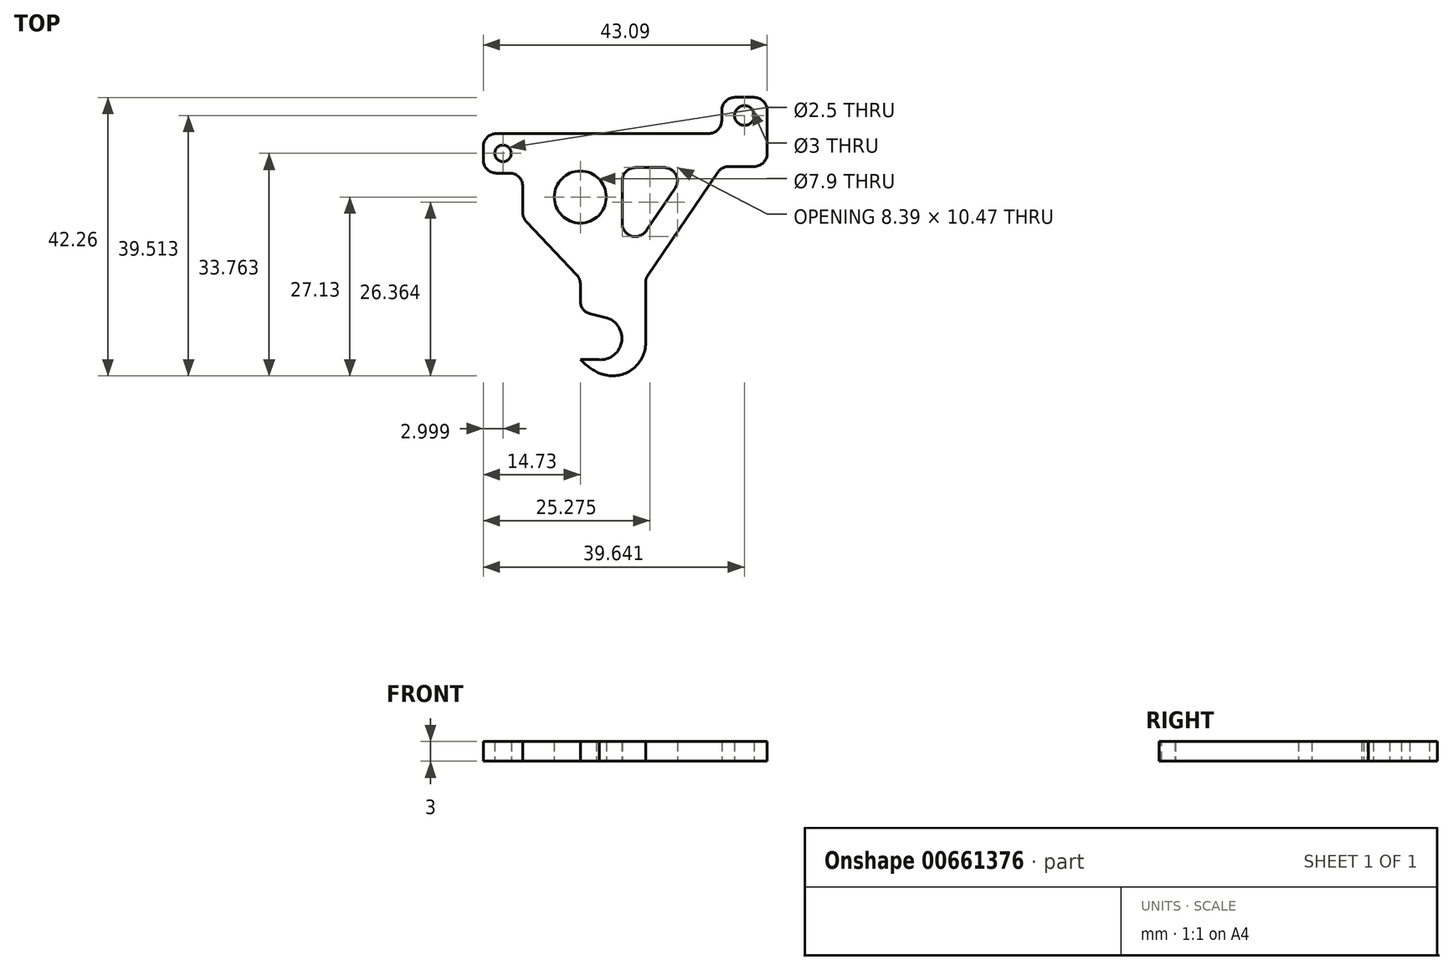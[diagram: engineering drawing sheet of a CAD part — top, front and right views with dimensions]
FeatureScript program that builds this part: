
annotation { "Feature Type Name" : "Feature", "Feature Type Description" : "" }
export const myFeature = defineFeature(function(context is Context, id is Id, definition is map)
    precondition{}
    {
        {
            var Q0;
            Q0=qCreatedBy(makeId("Top.planeOp"),FACE);
            var sketch = newSketch(context, id + "F0", { "sketchPlane" : qUnion([Q0])});
            skLineSegment(sketch, "E0.bottom", {"start": v(9.91, -14.86) * mm, "end": v(4.02, -14.86) * mm});
            skLineSegment(sketch, "E0.top", {"start": v(21.46, 22.01) * mm, "end": v(-8.73, 22.01) * mm});
            skPoint(sketch, "E0.middle", {"position": v(0, 0) * mm});
            skCircle(sketch, "E1", {"center": v(0, 12.38) * mm, "radius": 3.95 * mm});
            skLineSegment(sketch, "E2", {"start": v(9.91, -11.44) * mm, "end": v(9.91, -14.86) * mm});
            skLineSegment(sketch, "E3", {"start": v(-8.73, 9.2) * mm, "end": v(-8.76, 9.2) * mm});
            skLineSegment(sketch, "E4", {"start": v(28.36, 17.01) * mm, "end": v(21.46, 17.01) * mm});
            skLineSegment(sketch, "E5", {"start": v(21.46, 17.01) * mm, "end": v(9.91, 0) * mm});
            skLineSegment(sketch, "E6", {"start": v(9.91, 0) * mm, "end": v(9.91, -11.44) * mm});
            skLineSegment(sketch, "E7", {"start": v(0, -13.25) * mm, "end": v(0, -12.25) * mm});
            skLineSegment(sketch, "E8", {"start": v(0, -5) * mm, "end": v(0, 0) * mm});
            skLineSegment(sketch, "E9", {"start": v(0, 0) * mm, "end": v(-8.73, 9.2) * mm});
            skLineSegment(sketch, "E10", {"start": v(-8.73, 17.01) * mm, "end": v(-8.73, 9.2) * mm});
            skArc(sketch, "E11", {"start": v(2.43, -12.25) * mm, "mid": v(6.24, -9.75) * mm, "end": v(3.8, -5.9) * mm});
            skLineSegment(sketch, "E12", {"start": v(3.7, -12.25) * mm, "end": v(0, -12.25) * mm});
            skLineSegment(sketch, "E13", {"start": v(0, -5) * mm, "end": v(3.8, -5.9) * mm});
            skLineSegment(sketch, "E14", {"start": v(0, -13.25) * mm, "end": v(4.02, -14.86) * mm});
            skLineSegment(sketch, "E15.2", {"start": v(16.52, 16.85) * mm, "end": v(6.35, 1.87) * mm});
            skLineSegment(sketch, "E16", {"start": v(16.52, 16.85) * mm, "end": v(6.35, 16.85) * mm});
            skLineSegment(sketch, "E17", {"start": v(6.35, 16.85) * mm, "end": v(6.35, 1.87) * mm});
            skLineSegment(sketch, "E18.bottom", {"start": v(-8.73, 22.01) * mm, "end": v(-14.73, 22.01) * mm});
            skLineSegment(sketch, "E18.top", {"start": v(-8.73, 16.01) * mm, "end": v(-14.73, 16.01) * mm});
            skLineSegment(sketch, "E18.left", {"start": v(-8.73, 17.01) * mm, "end": v(-8.73, 16.01) * mm});
            skLineSegment(sketch, "E18.right", {"start": v(-14.73, 22.01) * mm, "end": v(-14.73, 16.01) * mm});
            skCircle(sketch, "E19", {"center": v(-11.73, 19.01) * mm, "radius": 1.25 * mm});
            skLineSegment(sketch, "E20.top", {"start": v(21.46, 27.51) * mm, "end": v(28.36, 27.51) * mm});
            skLineSegment(sketch, "E20.left", {"start": v(21.46, 22.01) * mm, "end": v(21.46, 27.51) * mm});
            skLineSegment(sketch, "E20.right", {"start": v(28.36, 22.01) * mm, "end": v(28.36, 27.51) * mm});
            skLineSegment(sketch, "E21", {"start": v(28.36, 22.01) * mm, "end": v(28.36, 17.01) * mm});
            skCircle(sketch, "E22", {"center": v(24.91, 24.76) * mm, "radius": 1.5 * mm});
            skPoint(sketch, "E22.centerSnap0", {"position": v(24.91, 27.51) * mm});
            skPoint(sketch, "E22.centerSnap1", {"position": v(21.46, 24.76) * mm});
            skSolve(sketch);
        }
        {
            var Q0;
            Q0=makeQuery(id+"F0.imprint","IMPRINT",FACE,{"disambiguationData":[TD([[makeQuery(id+"F0.imprint","IMPRINT",EDGE,{"derivedFrom":sQuery(id+"F0.wireOp",EDGE,"E0.top")}),1.0]])]});
            extrude(context, id + "F1", {"entities" : qUnion([Q0]), "depth" : 3 * mm, "offsetDistance" : 25 * mm});
        }
        {
            var Q0;
            Q0=makeQuery(id+"F1.opExtrude","SWEPT_EDGE",EDGE,{"disambiguationData":[OSD([sQuery(id+"F0.wireOp",EDGE,"E0.bottom"),sQuery(id+"F0.wireOp",EDGE,"E14")])]});
            fillet(context, id + "F2", {"entities" : qUnion([Q0]), "radius" : 10 * mm, "tangentPropagation" : true, "allowEdgeOverflow" : false});
        }
        {
            var Q0;
            Q0=makeQuery(id+"F1.opExtrude","SWEPT_EDGE",EDGE,{"disambiguationData":[OSD([sQuery(id+"F0.wireOp",EDGE,"E0.top"),sQuery(id+"F0.wireOp",EDGE,"E0.left")])]});
            var Q1;
            Q1=makeQuery(id+"F1.opExtrude","SWEPT_EDGE",EDGE,{"disambiguationData":[OSD([sQuery(id+"F0.wireOp",EDGE,"E0.top"),sQuery(id+"F0.wireOp",EDGE,"pHyUVdDd-3h7J-JCKs-Me8h-KnZJbw5tkJAh")])]});
            var Q2;
            Q2=makeQuery(id+"F1.opExtrude","SWEPT_EDGE",EDGE,{"disambiguationData":[OSD([sQuery(id+"F0.wireOp",EDGE,"OhQo3RvB-VFTn-GXlj-3DeX-jnrqFRKcEsYa"),sQuery(id+"F0.wireOp",EDGE,"pHyUVdDd-3h7J-JCKs-Me8h-KnZJbw5tkJAh")])]});
            var Q3;
            Q3=makeQuery(id+"F1.opExtrude","SWEPT_EDGE",EDGE,{"disambiguationData":[OSD([sQuery(id+"F0.wireOp",EDGE,"E10"),sQuery(id+"F0.wireOp",EDGE,"OhQo3RvB-VFTn-GXlj-3DeX-jnrqFRKcEsYa")])]});
            var Q4;
            Q4=makeQuery(id+"F1.opExtrude","SWEPT_EDGE",EDGE,{"disambiguationData":[OSD([sQuery(id+"F0.wireOp",EDGE,"E4"),sQuery(id+"F0.wireOp",EDGE,"E5")])]});
            var Q5;
            Q5=makeQuery(id+"F1.opExtrude","SWEPT_EDGE",EDGE,{"disambiguationData":[OSD([sQuery(id+"F0.wireOp",EDGE,"E9"),sQuery(id+"F0.wireOp",EDGE,"E10")])]});
            var Q6;
            Q6=makeQuery(id+"F1.opExtrude","SWEPT_EDGE",EDGE,{"disambiguationData":[OSD([sQuery(id+"F0.wireOp",EDGE,"E8"),sQuery(id+"F0.wireOp",EDGE,"E9")])]});
            var Q7;
            Q7=makeQuery(id+"F1.opExtrude","SWEPT_EDGE",EDGE,{"disambiguationData":[OSD([sQuery(id+"F0.wireOp",EDGE,"E8"),sQuery(id+"F0.wireOp",EDGE,"E13")])]});
            var Q8;
            Q8=makeQuery(id+"F1.opExtrude","SWEPT_EDGE",EDGE,{"disambiguationData":[OSD([sQuery(id+"F0.wireOp",EDGE,"E5"),sQuery(id+"F0.wireOp",EDGE,"E6")])]});
            var Q9;
            Q9=makeQuery(id+"F1.opExtrude","SWEPT_EDGE",EDGE,{"disambiguationData":[OSD([sQuery(id+"F0.wireOp",EDGE,"E0.left"),sQuery(id+"F0.wireOp",EDGE,"E4")])]});
            var Q10;
            Q10=makeQuery(id+"F1.opExtrude","SWEPT_EDGE",EDGE,{"disambiguationData":[OSD([sQuery(id+"F0.wireOp",EDGE,"E16"),sQuery(id+"F0.wireOp",EDGE,"E17")])]});
            var Q11;
            Q11=makeQuery(id+"F1.opExtrude","SWEPT_EDGE",EDGE,{"disambiguationData":[OSD([sQuery(id+"F0.wireOp",EDGE,"E15.2"),sQuery(id+"F0.wireOp",EDGE,"E16")])]});
            var Q12;
            Q12=makeQuery(id+"F1.opExtrude","SWEPT_EDGE",EDGE,{"disambiguationData":[OSD([sQuery(id+"F0.wireOp",EDGE,"E15.2"),sQuery(id+"F0.wireOp",EDGE,"E17")])]});
            var Q13;
            Q13=makeQuery(id+"F1.opExtrude","SWEPT_EDGE",EDGE,{"disambiguationData":[OSD([sQuery(id+"F0.wireOp",EDGE,"E18.top"),sQuery(id+"F0.wireOp",EDGE,"E18.right")])]});
            var Q14;
            Q14=makeQuery(id+"F1.opExtrude","SWEPT_EDGE",EDGE,{"disambiguationData":[OSD([sQuery(id+"F0.wireOp",EDGE,"E18.bottom"),sQuery(id+"F0.wireOp",EDGE,"E18.right")])]});
            var Q15;
            Q15=makeQuery(id+"F1.opExtrude","SWEPT_EDGE",EDGE,{"disambiguationData":[OSD([sQuery(id+"F0.wireOp",EDGE,"Wf6xNexR-8VgF-dvem-LY5D-CjuGMFQnJtrr"),sQuery(id+"F0.wireOp",EDGE,"B4st1OD0-YX5B-bgBp-xqhk-wKI3aAEfzf1H")])]});
            var Q16;
            Q16=makeQuery(id+"F1.opExtrude","SWEPT_EDGE",EDGE,{"disambiguationData":[OSD([sQuery(id+"F0.wireOp",EDGE,"B4st1OD0-YX5B-bgBp-xqhk-wKI3aAEfzf1H"),sQuery(id+"F0.wireOp",EDGE,"RDjMmuDR-6cde-Gaga-eYnt-srqOp1SnWC0k")])]});
            var Q17;
            Q17=makeQuery(id+"F1.opExtrude","SWEPT_EDGE",EDGE,{"disambiguationData":[OSD([sQuery(id+"F0.wireOp",EDGE,"E20.top"),sQuery(id+"F0.wireOp",EDGE,"E20.right")])]});
            var Q18;
            Q18=makeQuery(id+"F1.opExtrude","SWEPT_EDGE",EDGE,{"disambiguationData":[OSD([sQuery(id+"F0.wireOp",EDGE,"E20.top"),sQuery(id+"F0.wireOp",EDGE,"E20.left")])]});
            fillet(context, id + "F3", {"entities" : qUnion([Q0, Q1, Q2, Q3, Q4, Q5, Q6, Q7, Q8, Q9, Q10, Q11, Q12, Q13, Q14, Q15, Q16, Q17, Q18]), "radius" : 2 * mm, "tangentPropagation" : true, "allowEdgeOverflow" : false});
        }
        {
            var Q0;
            Q0=makeQuery(id+"F1.opExtrude","SWEPT_EDGE",EDGE,{"disambiguationData":[OSD([sQuery(id+"F0.wireOp",EDGE,"E7"),sQuery(id+"F0.wireOp",EDGE,"E14")])]});
            var Q1;
            Q1=makeQuery(id+"F1.opExtrude","SWEPT_EDGE",EDGE,{"disambiguationData":[OSD([sQuery(id+"F0.wireOp",EDGE,"E2"),sQuery(id+"F0.wireOp",EDGE,"E0.bottom")])]});
            fillet(context, id + "F4", {"entities" : qUnion([Q0, Q1]), "radius" : 5 * mm, "tangentPropagation" : true, "allowEdgeOverflow" : false});
        }
    });
